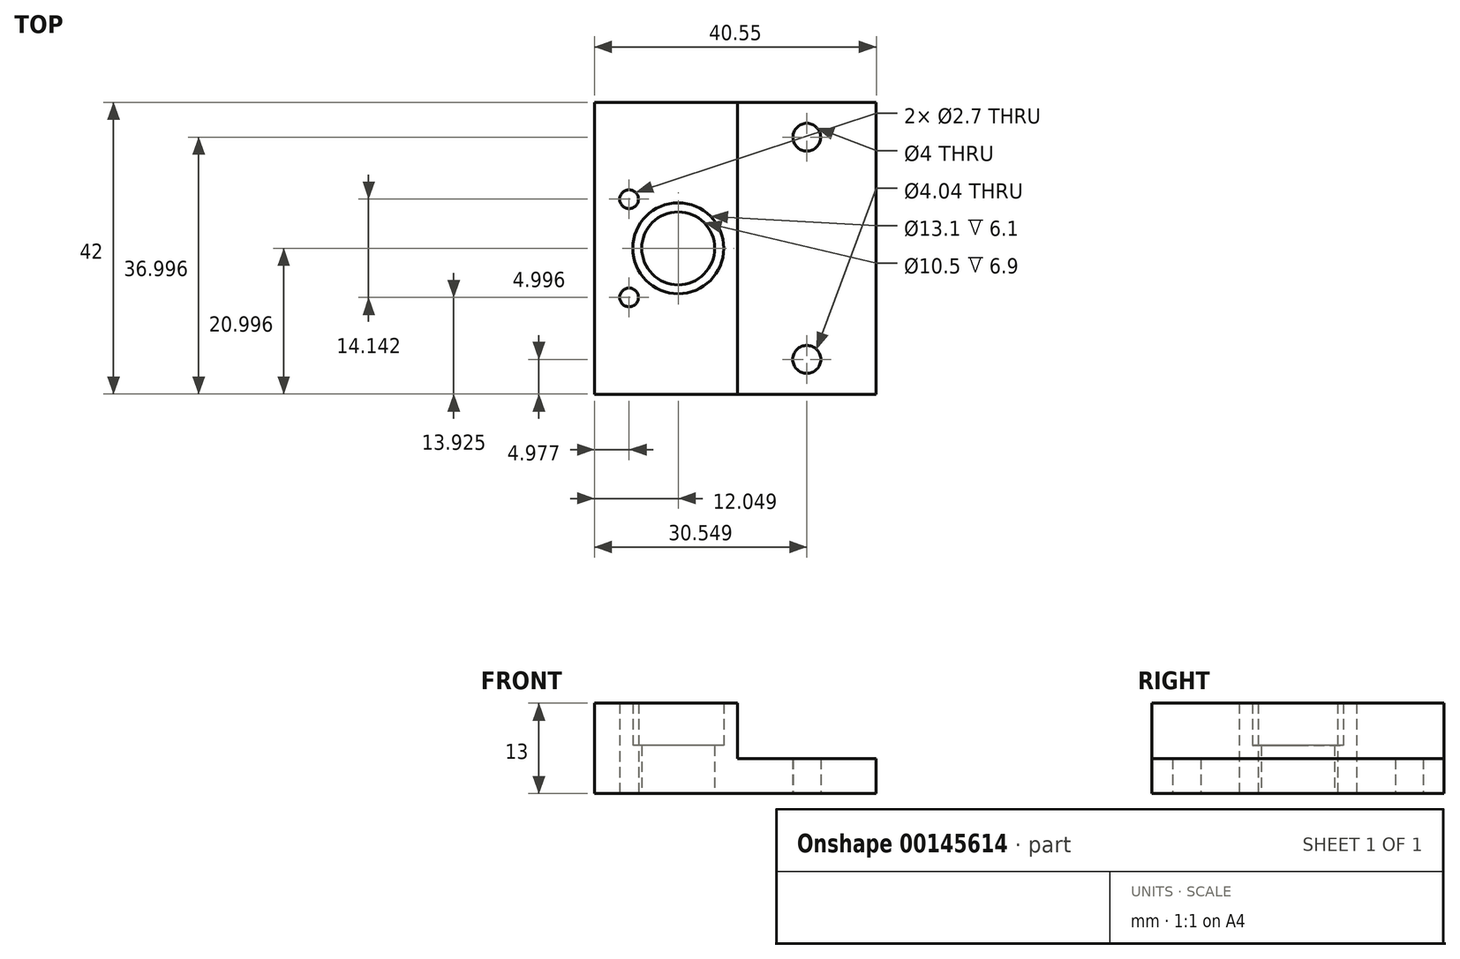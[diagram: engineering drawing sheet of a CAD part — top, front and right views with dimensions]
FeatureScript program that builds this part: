
annotation { "Feature Type Name" : "Feature", "Feature Type Description" : "" }
export const myFeature = defineFeature(function(context is Context, id is Id, definition is map)
    precondition{}
    {
        {
            var Q0;
            Q0=qCreatedBy(makeId("Top.planeOp"),FACE);
            var sketch = newSketch(context, id + "F0", { "sketchPlane" : qUnion([Q0])});
            skLineSegment(sketch, "E0.bottom", {"start": v(-17.1, 35.17) * mm, "end": v(23.46, 35.17) * mm});
            skLineSegment(sketch, "E0.top", {"start": v(-17.1, -6.83) * mm, "end": v(23.46, -6.83) * mm});
            skLineSegment(sketch, "E0.left", {"start": v(-17.1, 35.17) * mm, "end": v(-17.1, -6.83) * mm});
            skLineSegment(sketch, "E0.right", {"start": v(23.46, 35.17) * mm, "end": v(23.46, -6.83) * mm});
            skLineSegment(sketch, "E1", {"start": v(13.46, 35.17) * mm, "end": v(13.46, -6.83) * mm, "construction": true});
            skLineSegment(sketch, "E2", {"start": v(-17.1, 14.17) * mm, "end": v(23.46, 14.17) * mm, "construction": true});
            skLineSegment(sketch, "E3", {"start": v(-5.04, 35.17) * mm, "end": v(-5.04, -6.83) * mm, "construction": true});
            skPoint(sketch, "E4", {"position": v(-5.04, 14.17) * mm});
            skLineSegment(sketch, "E5", {"start": v(-5.04, 14.17) * mm, "end": v(-12.11, 21.24) * mm, "construction": true});
            skLineSegment(sketch, "E6", {"start": v(-5.04, 14.17) * mm, "end": v(-12.11, 7.1) * mm, "construction": true});
            skCircle(sketch, "E7", {"center": v(13.46, 30.17) * mm, "radius": 2 * mm});
            skCircle(sketch, "E8", {"center": v(13.46, -1.83) * mm, "radius": 2.02 * mm});
            skCircle(sketch, "E9", {"center": v(-12.11, 21.24) * mm, "radius": 1.35 * mm});
            skCircle(sketch, "E10", {"center": v(-12.11, 7.1) * mm, "radius": 1.35 * mm});
            skCircle(sketch, "E11", {"center": v(-5.04, 14.17) * mm, "radius": 6.55 * mm});
            skLineSegment(sketch, "E12", {"start": v(3.46, 35.17) * mm, "end": v(3.46, -6.83) * mm});
            skCircle(sketch, "E13", {"center": v(-5.04, 14.17) * mm, "radius": 5.25 * mm});
            skSolve(sketch);
        }
        {
            var Q0;
            {var subQ0=sQuery(id+"F0.wireOp",EDGE,"E0.right");Q0=makeQuery(id+"F0.imprint","IMPRINT",FACE,{"disambiguationData":[TD([[makeQuery(id+"F0.imprint","IMPRINT",EDGE,{"derivedFrom":subQ0}),-1.0]])]});}
            extrude(context, id + "F1", {"entities" : qUnion([Q0]), "depth" : 5 * mm});
        }
        {
            var Q0;
            {var subQ0=sQuery(id+"F0.wireOp",EDGE,"E0.left");Q0=makeQuery(id+"F0.imprint","IMPRINT",FACE,{"disambiguationData":[TD([[makeQuery(id+"F0.imprint","IMPRINT",EDGE,{"derivedFrom":subQ0}),1.0]])]});}
            extrude(context, id + "F2", {"entities" : qUnion([Q0]), "operationType" : NewBodyOperationType.ADD, "depth" : (8 + 5) * mm});
        }
        {
            var Q0;
            Q0=makeQuery(id+"F0.imprint","IMPRINT",FACE,{"disambiguationData":[TD([[makeQuery(id+"F0.imprint","IMPRINT",EDGE,{"derivedFrom":sQuery(id+"F0.wireOp",EDGE,"E11")}),1.0]])]});
            extrude(context, id + "F3", {"entities" : qUnion([Q0]), "operationType" : NewBodyOperationType.ADD, "depth" : (5 + 8 - 6.1) * mm});
        }
    });
